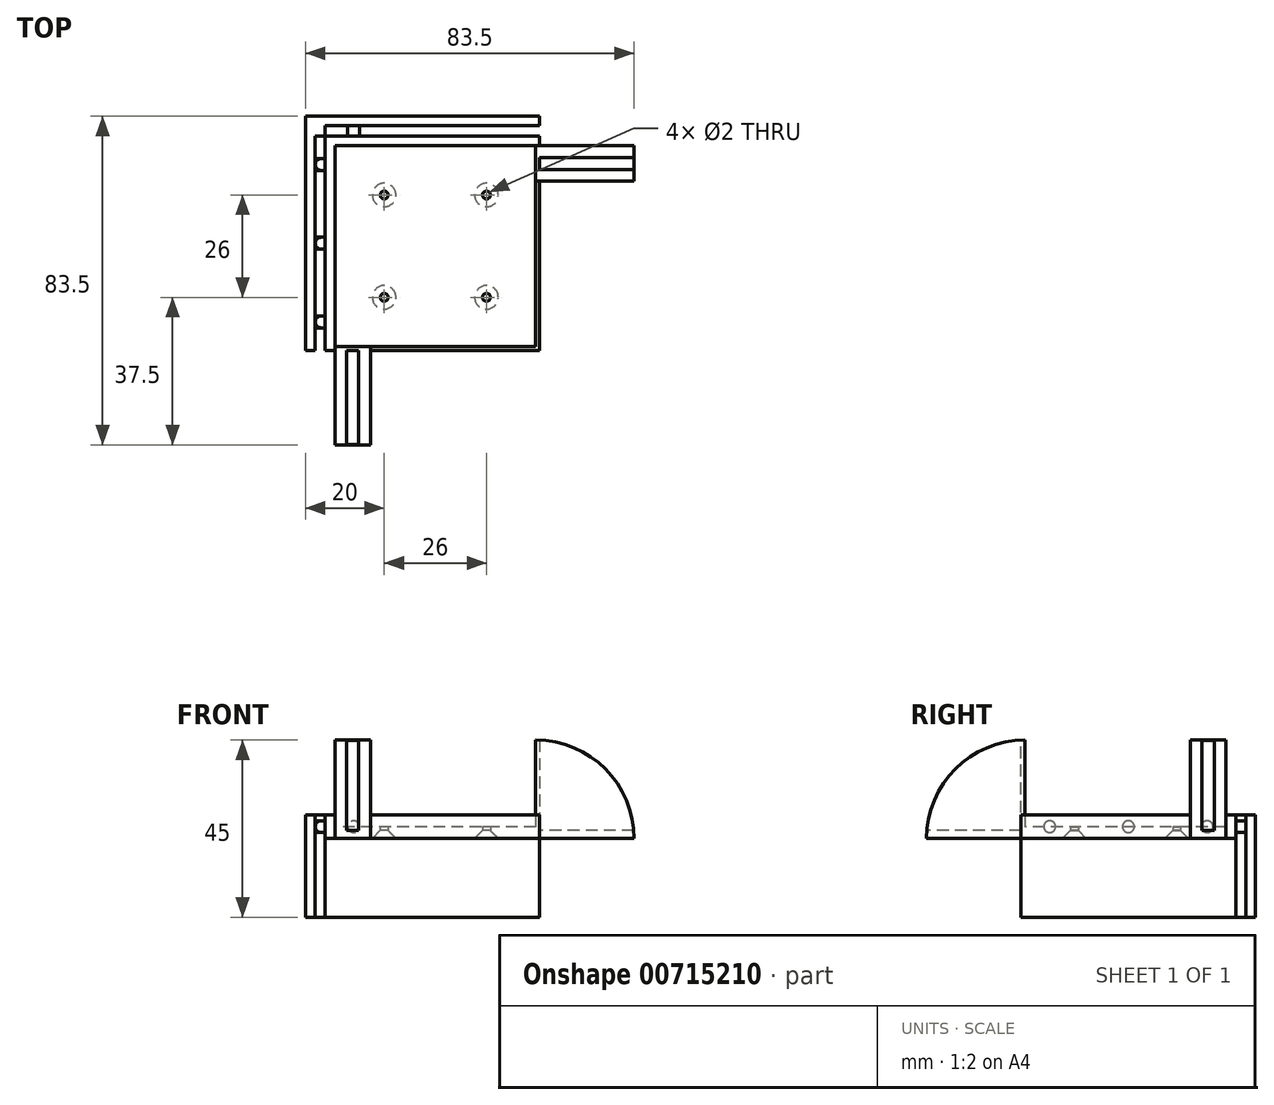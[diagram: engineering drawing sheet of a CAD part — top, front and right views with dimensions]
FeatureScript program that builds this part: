
annotation { "Feature Type Name" : "Feature", "Feature Type Description" : "" }
export const myFeature = defineFeature(function(context is Context, id is Id, definition is map)
    precondition{}
    {
        {
            var Q0;
            Q0=qCreatedBy(makeId("Top.planeOp"),FACE);
            var sketch = newSketch(context, id + "F0", { "sketchPlane" : qUnion([Q0])});
            skLineSegment(sketch, "E0.bottom", {"start": v(25.5, 25.5) * mm, "end": v(-25.5, 25.5) * mm});
            skLineSegment(sketch, "E0.top", {"start": v(25.5, -25.5) * mm, "end": v(-22.25, -25.5) * mm});
            skLineSegment(sketch, "E0.left", {"start": v(25.5, 25.5) * mm, "end": v(25.5, -25.5) * mm});
            skLineSegment(sketch, "E0.right", {"start": v(-25.5, 25.5) * mm, "end": v(-25.5, -25.5) * mm});
            skPoint(sketch, "E0.middle", {"position": v(0, 0) * mm});
            skLineSegment(sketch, "E1.0", {"start": v(28, 28) * mm, "end": v(-28, 28) * mm});
            skLineSegment(sketch, "E1.1", {"start": v(28, 28) * mm, "end": v(28, -28) * mm});
            skLineSegment(sketch, "E1.2", {"start": v(28, -28) * mm, "end": v(-22.25, -28) * mm});
            skLineSegment(sketch, "E1.3", {"start": v(-28, 28) * mm, "end": v(-28, -28) * mm});
            skCircle(sketch, "E2", {"center": v(-13, 13) * mm, "radius": 1 * mm});
            skLineSegment(sketch, "E3", {"start": v(0, 28) * mm, "end": v(0, -28) * mm, "construction": true});
            skLineSegment(sketch, "E4", {"start": v(-28, 0) * mm, "end": v(28, 0) * mm, "construction": true});
            skCircle(sketch, "E5.MirrorC", {"center": v(13, 13) * mm, "radius": 1 * mm});
            skCircle(sketch, "E6.MirrorC", {"center": v(13, -13) * mm, "radius": 1 * mm});
            skCircle(sketch, "E7.MirrorC", {"center": v(-13, -13) * mm, "radius": 1 * mm});
            skLineSegment(sketch, "E8.1", {"start": v(28, 33) * mm, "end": v(-33, 33) * mm});
            skLineSegment(sketch, "E9", {"start": v(28, 33) * mm, "end": v(28, 28) * mm});
            skLineSegment(sketch, "E10", {"start": v(-28, -28) * mm, "end": v(-33, -28) * mm});
            skLineSegment(sketch, "E11", {"start": v(28, 23.2) * mm, "end": v(28, 12.96) * mm});
            skLineSegment(sketch, "E12", {"start": v(28, 23.2) * mm, "end": v(28, 20) * mm});
            skLineSegment(sketch, "E13.trimOffspring", {"start": v(-25.25, -28) * mm, "end": v(-28, -28) * mm});
            skLineSegment(sketch, "E14", {"start": v(-25.5, -25.5) * mm, "end": v(-22.25, -25.5) * mm});
            skLineSegment(sketch, "E15", {"start": v(-25.25, -28) * mm, "end": v(-22.25, -28) * mm});
            skCircle(sketch, "E16", {"center": v(0, 0) * mm, "radius": 4.25 * mm});
            skLineSegment(sketch, "E17", {"start": v(-33, 33) * mm, "end": v(-33, -28) * mm});
            skSolve(sketch);
        }
        {
            var Q0;
            Q0=qCreatedBy(makeId("Top.planeOp"),FACE);
            var sketch = newSketch(context, id + "F1", { "sketchPlane" : qUnion([Q0])});
            skPoint(sketch, "E18.0", {"position": v(-25.5, -25.5) * mm});
            skLineSegment(sketch, "E19.bottom", {"start": v(-25.5, -25.5) * mm, "end": v(-16.5, -25.5) * mm});
            skLineSegment(sketch, "E19.top", {"start": v(-25.5, -50.5) * mm, "end": v(-16.5, -50.5) * mm});
            skLineSegment(sketch, "E19.left", {"start": v(-25.5, -25.5) * mm, "end": v(-25.5, -50.5) * mm});
            skLineSegment(sketch, "E19.right", {"start": v(-16.5, -25.5) * mm, "end": v(-16.5, -50.5) * mm});
            skLineSegment(sketch, "E20", {"start": v(-21, -50.5) * mm, "end": v(-21, -25.5) * mm, "construction": true});
            skLineSegment(sketch, "E21", {"start": v(-19.45, -25.5) * mm, "end": v(-19.45, -50.5) * mm});
            skLineSegment(sketch, "E22.MirrorCS", {"start": v(-22.55, -25.5) * mm, "end": v(-22.55, -50.5) * mm});
            skPoint(sketch, "E23.0", {"position": v(25.5, 25.5) * mm});
            skLineSegment(sketch, "E24.bottom", {"start": v(25.5, 25.5) * mm, "end": v(50.5, 25.5) * mm});
            skLineSegment(sketch, "E24.top", {"start": v(25.5, 16.5) * mm, "end": v(50.5, 16.5) * mm});
            skLineSegment(sketch, "E24.left", {"start": v(25.5, 25.5) * mm, "end": v(25.5, 16.5) * mm});
            skLineSegment(sketch, "E24.right", {"start": v(50.5, 25.5) * mm, "end": v(50.5, 16.5) * mm});
            skLineSegment(sketch, "E25", {"start": v(25.5, 21) * mm, "end": v(50.5, 21) * mm, "construction": true});
            skLineSegment(sketch, "E26", {"start": v(50.5, 22.55) * mm, "end": v(25.5, 22.55) * mm});
            skLineSegment(sketch, "E27.MirrorCS", {"start": v(50.5, 19.45) * mm, "end": v(25.5, 19.45) * mm});
            skSolve(sketch);
        }
        {
            var Q0;
            Q0=makeQuery(id+"F0.imprint","IMPRINT",FACE,{"disambiguationData":[TD([[makeQuery(id+"F0.imprint","IMPRINT",EDGE,{"derivedFrom":sQuery(id+"F0.wireOp",EDGE,"E0.bottom")}),1.0]])]});
            var Q1;
            Q1=makeQuery(id+"F0.imprint","IMPRINT",FACE,{"disambiguationData":[TD([[makeQuery(id+"F0.imprint","IMPRINT",EDGE,{"derivedFrom":sQuery(id+"F0.wireOp",EDGE,"E16")}),1.0]])]});
            extrude(context, id + "F2", {"entities" : qUnion([Q0, Q1]), "depth" : 3 * mm, "offsetDistance" : 25 * mm});
        }
        {
            var Q0;
            Q0=makeQuery(id+"F0.imprint","IMPRINT",FACE,{"disambiguationData":[TD([[makeQuery(id+"F0.imprint","IMPRINT",EDGE,{"derivedFrom":sQuery(id+"F0.wireOp",EDGE,"E0.bottom")}),-1.0]])]});
            var Q1;
            {var subQ5=sQuery(id+"F0.wireOp",EDGE,"TI18WCdd-EPFC-hNpH-Rctt-afuqL8Zf6Xfq");Q1=makeQuery(id+"F0.imprint","IMPRINT",FACE,{"disambiguationData":[TD([[makeQuery(id+"F0.imprint","IMPRINT",EDGE,{"derivedFrom":subQ5}),-1.0]])]});}
            extrude(context, id + "F3", {"entities" : qUnion([Q0, Q1]), "operationType" : NewBodyOperationType.ADD, "depth" : 6 * mm, "offsetDistance" : 25 * mm});
        }
        {
            var Q0;
            Q0=makeQuery(id+"F2.opExtrude","CAP_EDGE",EDGE,{"disambiguationData":[OSD([sQuery(id+"F0.wireOp",EDGE,"E7.MirrorC")])],"isStart":true});
            var Q1;
            Q1=makeQuery(id+"F2.opExtrude","CAP_EDGE",EDGE,{"disambiguationData":[OSD([sQuery(id+"F0.wireOp",EDGE,"E6.MirrorC")])],"isStart":true});
            var Q2;
            Q2=makeQuery(id+"F2.opExtrude","CAP_EDGE",EDGE,{"disambiguationData":[OSD([sQuery(id+"F0.wireOp",EDGE,"E5.MirrorC")])],"isStart":true});
            var Q3;
            Q3=makeQuery(id+"F2.opExtrude","CAP_EDGE",EDGE,{"disambiguationData":[OSD([sQuery(id+"F0.wireOp",EDGE,"E2")])],"isStart":true});
            chamfer(context, id + "F4", {"entities" : qUnion([Q0, Q1, Q2, Q3]), "width" : 2 * mm, "tangentPropagation" : true});
        }
        {
            var Q0;
            Q0=makeQuery(id+"FIbiUBh41szAzK7_1.boolean.opBoolean","MERGE",FACE,{"derivedFrom":[makeQuery(id+"F3.opExtrude","SWEPT_FACE",FACE,{"disambiguationData":[OSD([sQuery(id+"F0.wireOp",EDGE,"E1.2"),sQuery(id+"F0.wireOp",EDGE,"E13.trimOffspring"),sQuery(id+"F0.wireOp",EDGE,"E15")])]}),makeQuery(id+"FIbiUBh41szAzK7_1.opExtrude","SWEPT_FACE",FACE,{"disambiguationData":[OSD([sQuery(id+"F0.wireOp",EDGE,"E10")])]})]});
            extrude(context, id + "F5", {"entities" : qUnion([Q0]), "operationType" : NewBodyOperationType.REMOVE, "oppositeDirection" : true, "depth" : 1.5 * mm, "offsetDistance" : 25 * mm});
        }
        {
            var Q0;
            Q0=makeQuery(id+"FIbiUBh41szAzK7_1.boolean.opBoolean","MERGE",FACE,{"derivedFrom":[makeQuery(id+"F3.opExtrude","SWEPT_FACE",FACE,{"disambiguationData":[OSD([sQuery(id+"F0.wireOp",EDGE,"E1.1"),sQuery(id+"F0.wireOp",EDGE,"E11"),sQuery(id+"F0.wireOp",EDGE,"E12")])]}),makeQuery(id+"FIbiUBh41szAzK7_1.opExtrude","SWEPT_FACE",FACE,{"disambiguationData":[OSD([sQuery(id+"F0.wireOp",EDGE,"E9")])]})]});
            extrude(context, id + "F6", {"entities" : qUnion([Q0]), "operationType" : NewBodyOperationType.REMOVE, "oppositeDirection" : true, "depth" : 1.5 * mm, "offsetDistance" : 25 * mm});
        }
        {
            var Q0;
            {var subQ0=sQuery(id+"F1.wireOp",EDGE,"E19.right");Q0=makeQuery(id+"F1.imprint","IMPRINT",FACE,{"disambiguationData":[TD([[makeQuery(id+"F1.imprint","IMPRINT",EDGE,{"derivedFrom":subQ0}),-1.0]])]});}
            var Q1;
            {var subQ0=sQuery(id+"F1.wireOp",EDGE,"E19.left");Q1=makeQuery(id+"F1.imprint","IMPRINT",FACE,{"disambiguationData":[TD([[makeQuery(id+"F1.imprint","IMPRINT",EDGE,{"derivedFrom":subQ0}),1.0]])]});}
            var Q2;
            {var subQ0=sQuery(id+"F1.wireOp",EDGE,"E24.top");Q2=makeQuery(id+"F1.imprint","IMPRINT",FACE,{"disambiguationData":[TD([[makeQuery(id+"F1.imprint","IMPRINT",EDGE,{"derivedFrom":subQ0}),1.0]])]});}
            var Q3;
            {var subQ0=sQuery(id+"F1.wireOp",EDGE,"E24.bottom");Q3=makeQuery(id+"F1.imprint","IMPRINT",FACE,{"disambiguationData":[TD([[makeQuery(id+"F1.imprint","IMPRINT",EDGE,{"derivedFrom":subQ0}),-1.0]])]});}
            extrude(context, id + "F7", {"entities" : qUnion([Q0, Q1, Q2, Q3]), "operationType" : NewBodyOperationType.ADD, "depth" : 25 * mm, "offsetDistance" : 25 * mm});
        }
        {
            var Q0;
            {var subQ0=sQuery(id+"F1.wireOp",EDGE,"E21");Q0=makeQuery(id+"F1.imprint","IMPRINT",FACE,{"disambiguationData":[TD([[makeQuery(id+"F1.imprint","IMPRINT",EDGE,{"derivedFrom":subQ0}),-1.0]])]});}
            var Q1;
            {var subQ0=sQuery(id+"F1.wireOp",EDGE,"E26");Q1=makeQuery(id+"F1.imprint","IMPRINT",FACE,{"disambiguationData":[TD([[makeQuery(id+"F1.imprint","IMPRINT",EDGE,{"derivedFrom":subQ0}),1.0]])]});}
            extrude(context, id + "F8", {"entities" : qUnion([Q0, Q1]), "operationType" : NewBodyOperationType.ADD, "depth" : 2 * mm, "offsetDistance" : 25 * mm});
        }
        {
            var Q0;
            {var subQ1=sQuery(id+"F1.wireOp",EDGE,"E21");var subQ3=sQuery(id+"F0.wireOp",EDGE,"E15");var subQ4=sQuery(id+"F0.wireOp",EDGE,"E13.trimOffspring");var subQ5=sQuery(id+"F0.wireOp",EDGE,"E1.2");var subQ6=sQuery(id+"F0.wireOp",EDGE,"E14");var subQ7=sQuery(id+"F0.wireOp",EDGE,"E0.top");Q0=makeQuery(id+"F7.boolean.opBoolean","SPLIT",FACE,{"disambiguationData":[TD([makeQuery(id+"F7.opExtrude","SWEPT_FACE",FACE,{"disambiguationData":[OSD([subQ1])]})])],"derivedFrom":makeQuery(id+"F3.opExtrude","CAP_FACE",FACE,{"disambiguationData":[OSD([sQuery(id+"F0.wireOp",EDGE,"E0.bottom"),subQ7,sQuery(id+"F0.wireOp",EDGE,"E0.left"),sQuery(id+"F0.wireOp",EDGE,"E0.right"),sQuery(id+"F0.wireOp",EDGE,"E1.0"),sQuery(id+"F0.wireOp",EDGE,"E1.1"),subQ5,sQuery(id+"F0.wireOp",EDGE,"E1.3"),sQuery(id+"F0.wireOp",EDGE,"E11"),sQuery(id+"F0.wireOp",EDGE,"E12"),subQ4,subQ6,subQ3])],"isStart":false})});}
            var Q1;
            {var subQ1=sQuery(id+"F1.wireOp",EDGE,"E26");var subQ2=sQuery(id+"F0.wireOp",EDGE,"E12");var subQ3=sQuery(id+"F0.wireOp",EDGE,"E11");var subQ4=sQuery(id+"F0.wireOp",EDGE,"E1.1");var subQ6=sQuery(id+"F0.wireOp",EDGE,"E0.left");Q1=makeQuery(id+"F7.boolean.opBoolean","SPLIT",FACE,{"disambiguationData":[TD([makeQuery(id+"F7.opExtrude","SWEPT_FACE",FACE,{"disambiguationData":[OSD([subQ1])]})])],"derivedFrom":makeQuery(id+"F3.opExtrude","CAP_FACE",FACE,{"disambiguationData":[OSD([sQuery(id+"F0.wireOp",EDGE,"E0.bottom"),sQuery(id+"F0.wireOp",EDGE,"E0.top"),subQ6,sQuery(id+"F0.wireOp",EDGE,"E0.right"),sQuery(id+"F0.wireOp",EDGE,"E1.0"),subQ4,sQuery(id+"F0.wireOp",EDGE,"E1.2"),sQuery(id+"F0.wireOp",EDGE,"E1.3"),subQ3,subQ2,sQuery(id+"F0.wireOp",EDGE,"E13.trimOffspring"),sQuery(id+"F0.wireOp",EDGE,"E14"),sQuery(id+"F0.wireOp",EDGE,"E15")])],"isStart":false})});}
            var Q2;
            Q2=makeQuery(id+"F7.opExtrude","CAP_FACE",FACE,{"disambiguationData":[OSD([sQuery(id+"F1.wireOp",EDGE,"E19.bottom"),sQuery(id+"F1.wireOp",EDGE,"E19.top"),sQuery(id+"F1.wireOp",EDGE,"E19.left"),sQuery(id+"F1.wireOp",EDGE,"E22.MirrorCS")])],"isStart":false});
            var Q3;
            Q3=makeQuery(id+"F2.opExtrude","SWEPT_BODY",BODY,{"disambiguationData":[OSD([sQuery(id+"F0.wireOp",EDGE,"E0.bottom"),sQuery(id+"F0.wireOp",EDGE,"E0.top"),sQuery(id+"F0.wireOp",EDGE,"E0.left"),sQuery(id+"F0.wireOp",EDGE,"E0.right"),sQuery(id+"F0.wireOp",EDGE,"E2"),sQuery(id+"F0.wireOp",EDGE,"E5.MirrorC"),sQuery(id+"F0.wireOp",EDGE,"E6.MirrorC"),sQuery(id+"F0.wireOp",EDGE,"E7.MirrorC"),sQuery(id+"F0.wireOp",EDGE,"E14"),sQuery(id+"F0.wireOp",EDGE,"E16")])]});
            extrude(context, id + "F9", {"entities" : qUnion([Q0, Q1]), "operationType" : NewBodyOperationType.ADD, "endBound" : BoundingType.UP_TO_SURFACE, "depth" : 25 * mm, "endBoundEntityFace" : qUnion([Q2]), "endBoundEntityBody" : qUnion([Q3]), "offsetDistance" : 25 * mm});
        }
        {
            var Q0;
            {var subQ0=sQuery(id+"F1.wireOp",EDGE,"E19.top");Q0=makeQuery(id+"F7.opExtrude","CAP_EDGE",EDGE,{"disambiguationData":[OSD([subQ0]),TDD([makeQuery(id+"F1.imprint","IMPRINT",EDGE,{"disambiguationData":[TD([[makeQuery(id+"F1.imprint","INTERSECT",VERTEX,{"derivedFrom":[subQ0,sQuery(id+"F1.wireOp",EDGE,"E19.left")]}),-1.0]])],"derivedFrom":subQ0})])],"isStart":false});}
            var Q1;
            {var subQ0=sQuery(id+"F1.wireOp",EDGE,"E19.top");Q1=makeQuery(id+"F7.opExtrude","CAP_EDGE",EDGE,{"disambiguationData":[OSD([subQ0]),TDD([makeQuery(id+"F1.imprint","IMPRINT",EDGE,{"disambiguationData":[TD([[makeQuery(id+"F1.imprint","INTERSECT",VERTEX,{"derivedFrom":[subQ0,sQuery(id+"F1.wireOp",EDGE,"E19.right")]}),1.0]])],"derivedFrom":subQ0})])],"isStart":false});}
            var Q2;
            {var subQ0=sQuery(id+"F1.wireOp",EDGE,"E24.right");Q2=makeQuery(id+"F7.opExtrude","CAP_EDGE",EDGE,{"disambiguationData":[OSD([subQ0]),TDD([makeQuery(id+"F1.imprint","IMPRINT",EDGE,{"disambiguationData":[TD([[makeQuery(id+"F1.imprint","INTERSECT",VERTEX,{"derivedFrom":[sQuery(id+"F1.wireOp",EDGE,"E24.bottom"),subQ0]}),-1.0]])],"derivedFrom":subQ0})])],"isStart":false});}
            fillet(context, id + "F10", {"entities" : qUnion([Q0, Q1, Q2]), "radius" : 25 * mm, "tangentPropagation" : true, "allowEdgeOverflow" : false});
        }
        {
            var Q0;
            Q0=makeQuery(id+"F3.opExtrude","SWEPT_FACE",FACE,{"disambiguationData":[OSD([sQuery(id+"F0.wireOp",EDGE,"E1.3")])]});
            var sketch = newSketch(context, id + "F11", { "sketchPlane" : qUnion([Q0])});
            skCircle(sketch, "E28", {"center": v(-20.75, 3) * mm, "radius": 1.5 * mm});
            skPoint(sketch, "E28.centerSnap0", {"position": v(-28, 3) * mm});
            skCircle(sketch, "E29", {"center": v(19.25, 3) * mm, "radius": 1.5 * mm});
            skCircle(sketch, "E30", {"center": v(-0.75, 3) * mm, "radius": 1.5 * mm});
            skPoint(sketch, "E30.centerSnap0", {"position": v(-0.75, 6) * mm});
            skSolve(sketch);
        }
        {
            var Q0;
            Q0=makeQuery(id+"F11.imprint","IMPRINT",FACE,{"disambiguationData":[TD([[makeQuery(id+"F11.imprint","IMPRINT",EDGE,{"derivedFrom":sQuery(id+"F11.wireOp",EDGE,"E28")}),1.0]])]});
            var Q1;
            Q1=makeQuery(id+"F11.imprint","IMPRINT",FACE,{"disambiguationData":[TD([[makeQuery(id+"F11.imprint","IMPRINT",EDGE,{"derivedFrom":sQuery(id+"F11.wireOp",EDGE,"E30")}),1.0]])]});
            var Q2;
            Q2=makeQuery(id+"F11.imprint","IMPRINT",FACE,{"disambiguationData":[TD([[makeQuery(id+"F11.imprint","IMPRINT",EDGE,{"derivedFrom":sQuery(id+"F11.wireOp",EDGE,"E29")}),1.0]])]});
            extrude(context, id + "F12", {"entities" : qUnion([Q0, Q1, Q2]), "operationType" : NewBodyOperationType.ADD, "depth" : 2.5 * mm, "offsetDistance" : 25 * mm});
        }
        {
            var Q0;
            Q0=makeQuery(id+"F3.opExtrude","SWEPT_FACE",FACE,{"disambiguationData":[OSD([sQuery(id+"F0.wireOp",EDGE,"E1.0")])]});
            var sketch = newSketch(context, id + "F13", { "sketchPlane" : qUnion([Q0])});
            skCircle(sketch, "E31", {"center": v(0.75, 3) * mm, "radius": 1.5 * mm});
            skPoint(sketch, "E31.centerSnap0", {"position": v(28, 3) * mm});
            skPoint(sketch, "E31.centerSnap1", {"position": v(0.75, 6) * mm});
            skCircle(sketch, "E32", {"center": v(20.75, 3) * mm, "radius": 1.5 * mm});
            skCircle(sketch, "E33", {"center": v(-19.25, 3) * mm, "radius": 1.5 * mm});
            skSolve(sketch);
        }
        {
            var Q0;
            Q0=makeQuery(id+"F13.imprint","IMPRINT",FACE,{"disambiguationData":[TD([[makeQuery(id+"F13.imprint","IMPRINT",EDGE,{"derivedFrom":sQuery(id+"F13.wireOp",EDGE,"E33")}),1.0]])]});
            var Q1;
            Q1=makeQuery(id+"F13.imprint","IMPRINT",FACE,{"disambiguationData":[TD([[makeQuery(id+"F13.imprint","IMPRINT",EDGE,{"derivedFrom":sQuery(id+"F13.wireOp",EDGE,"E31")}),1.0]])]});
            extrude(context, id + "F14", {"entities" : qUnion([Q0, Q1]), "operationType" : NewBodyOperationType.ADD, "depth" : 2.5 * mm, "offsetDistance" : 25 * mm});
        }
        {
            var Q0;
            Q0=makeQuery(id+"F12.opExtrude","CAP_FACE",FACE,{"disambiguationData":[OSD([sQuery(id+"F11.wireOp",EDGE,"E28")])],"isStart":false});
            var Q1;
            Q1=makeQuery(id+"F12.opExtrude","CAP_FACE",FACE,{"disambiguationData":[OSD([sQuery(id+"F11.wireOp",EDGE,"E30")])],"isStart":false});
            var Q2;
            Q2=makeQuery(id+"F12.opExtrude","CAP_FACE",FACE,{"disambiguationData":[OSD([sQuery(id+"F11.wireOp",EDGE,"E29")])],"isStart":false});
            var Q3;
            Q3=makeQuery(id+"F14.opExtrude","CAP_FACE",FACE,{"disambiguationData":[OSD([sQuery(id+"F13.wireOp",EDGE,"E33")])],"isStart":false});
            var Q4;
            Q4=makeQuery(id+"F14.opExtrude","CAP_FACE",FACE,{"disambiguationData":[OSD([sQuery(id+"F13.wireOp",EDGE,"E31")])],"isStart":false});
            fillet(context, id + "F15", {"entities" : qUnion([Q0, Q1, Q2, Q3, Q4]), "radius" : 1.5 * mm, "tangentPropagation" : true, "allowEdgeOverflow" : false});
        }
        {
            var Q0;
            Q0=makeQuery(id+"F0.imprint","IMPRINT",FACE,{"disambiguationData":[TD([[makeQuery(id+"F0.imprint","IMPRINT",EDGE,{"derivedFrom":sQuery(id+"F0.wireOp",EDGE,"E1.0")}),-1.0]])]});
            extrude(context, id + "F16", {"entities" : qUnion([Q0]), "depth" : 6 * mm, "offsetDistance" : 25 * mm, "hasSecondDirection" : true, "secondDirectionOppositeDirection" : true, "secondDirectionDepth" : 20 * mm});
        }
        {
            var Q0;
            Q0=makeQuery(id+"F16.opExtrude","SWEPT_FACE",FACE,{"disambiguationData":[OSD([sQuery(id+"F0.wireOp",EDGE,"E9")])]});
            extrude(context, id + "F17", {"entities" : qUnion([Q0]), "operationType" : NewBodyOperationType.REMOVE, "oppositeDirection" : true, "depth" : 1.5 * mm, "offsetDistance" : 25 * mm});
        }
        {
            var Q0;
            Q0=makeQuery(id+"F16.opExtrude","SWEPT_FACE",FACE,{"disambiguationData":[OSD([sQuery(id+"F0.wireOp",EDGE,"E10")])]});
            extrude(context, id + "F18", {"entities" : qUnion([Q0]), "operationType" : NewBodyOperationType.REMOVE, "oppositeDirection" : true, "depth" : 1.5 * mm, "offsetDistance" : 25 * mm});
        }
        {
            var Q0;
            Q0=makeQuery(id+"F16.opExtrude","SWEPT_FACE",FACE,{"disambiguationData":[OSD([sQuery(id+"F0.wireOp",EDGE,"E1.3")])]});
            var sketch = newSketch(context, id + "F19", { "sketchPlane" : qUnion([Q0])});
            skCircle(sketch, "E34.0", {"center": v(20.75, 3) * mm, "radius": 1.5 * mm});
            skCircle(sketch, "E34.1", {"center": v(0.75, 3) * mm, "radius": 1.5 * mm});
            skCircle(sketch, "E34.2", {"center": v(-19.25, 3) * mm, "radius": 1.5 * mm});
            skSolve(sketch);
        }
        {
            var Q0;
            Q0=makeQuery(id+"F16.opExtrude","SWEPT_FACE",FACE,{"disambiguationData":[OSD([sQuery(id+"F0.wireOp",EDGE,"E1.0")])]});
            var sketch = newSketch(context, id + "F20", { "sketchPlane" : qUnion([Q0])});
            skCircle(sketch, "E35.0", {"center": v(-20.75, 3) * mm, "radius": 1.5 * mm});
            skCircle(sketch, "E35.1", {"center": v(-0.75, 3) * mm, "radius": 1.5 * mm});
            skCircle(sketch, "E35.2", {"center": v(19.25, 3) * mm, "radius": 1.5 * mm});
            skSolve(sketch);
        }
        {
            var Q0;
            Q0=makeQuery(id+"F20.imprint","IMPRINT",FACE,{"disambiguationData":[TD([[makeQuery(id+"F20.imprint","IMPRINT",EDGE,{"derivedFrom":sQuery(id+"F20.wireOp",EDGE,"E35.0")}),-1.0]])]});
            var Q1;
            Q1=makeQuery(id+"F13.imprint","IMPRINT",FACE,{"disambiguationData":[TD([[makeQuery(id+"F13.imprint","IMPRINT",EDGE,{"derivedFrom":sQuery(id+"F13.wireOp",EDGE,"E31")}),1.0]])]});
            var Q2;
            Q2=makeQuery(id+"F13.imprint","IMPRINT",FACE,{"disambiguationData":[TD([[makeQuery(id+"F13.imprint","IMPRINT",EDGE,{"derivedFrom":sQuery(id+"F13.wireOp",EDGE,"E33")}),1.0]])]});
            extrude(context, id + "F21", {"entities" : qUnion([Q0, Q1, Q2]), "operationType" : NewBodyOperationType.REMOVE, "oppositeDirection" : true, "depth" : 2.6 * mm, "offsetDistance" : 25 * mm});
        }
        {
            var Q0;
            Q0=makeQuery(id+"F19.imprint","IMPRINT",FACE,{"disambiguationData":[TD([[makeQuery(id+"F19.imprint","IMPRINT",EDGE,{"derivedFrom":sQuery(id+"F19.wireOp",EDGE,"E34.0")}),-1.0]])]});
            var Q1;
            Q1=makeQuery(id+"F19.imprint","IMPRINT",FACE,{"disambiguationData":[TD([[makeQuery(id+"F19.imprint","IMPRINT",EDGE,{"derivedFrom":sQuery(id+"F19.wireOp",EDGE,"E34.1")}),-1.0]])]});
            var Q2;
            Q2=makeQuery(id+"F19.imprint","IMPRINT",FACE,{"disambiguationData":[TD([[makeQuery(id+"F19.imprint","IMPRINT",EDGE,{"derivedFrom":sQuery(id+"F19.wireOp",EDGE,"E34.2")}),-1.0]])]});
            extrude(context, id + "F22", {"entities" : qUnion([Q0, Q1, Q2]), "operationType" : NewBodyOperationType.REMOVE, "oppositeDirection" : true, "depth" : 2.6 * mm, "offsetDistance" : 25 * mm});
        }
    });
